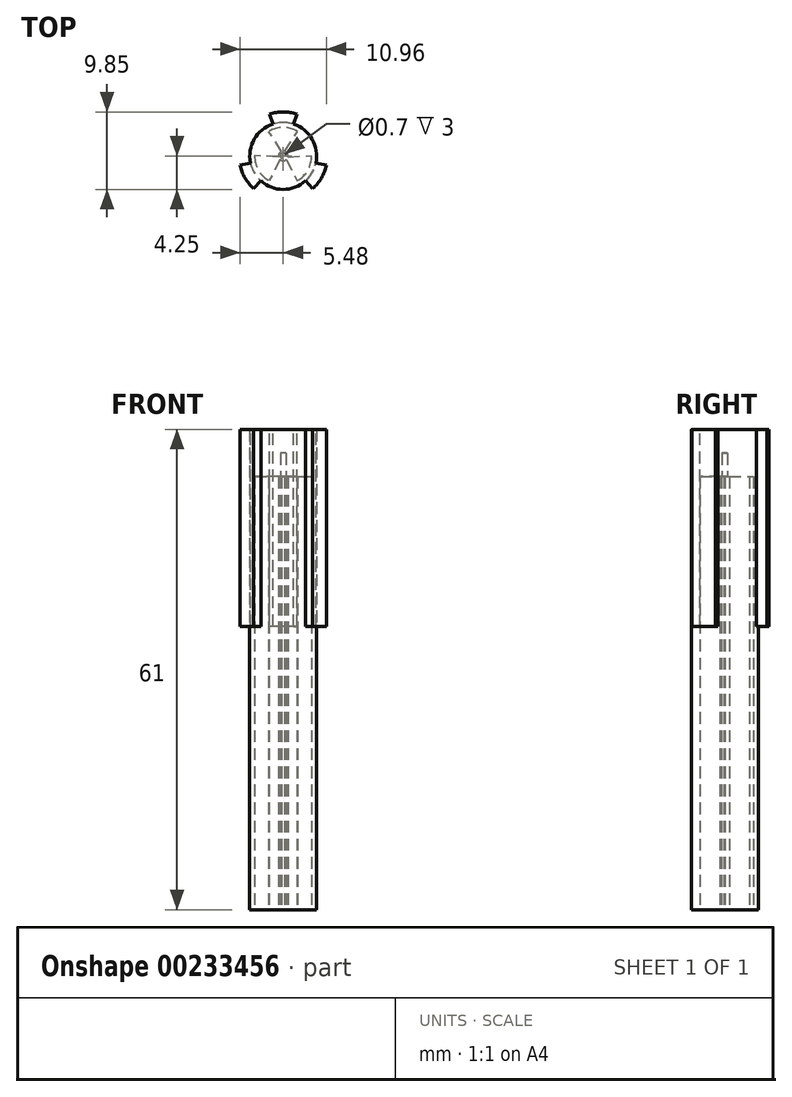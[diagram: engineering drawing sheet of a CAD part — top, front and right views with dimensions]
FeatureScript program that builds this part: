
annotation { "Feature Type Name" : "Feature", "Feature Type Description" : "" }
export const myFeature = defineFeature(function(context is Context, id is Id, definition is map)
    precondition{}
    {
        {
            var Q0;
            Q0=qCreatedBy(makeId("Top.planeOp"),FACE);
            var sketch = newSketch(context, id + "F0", { "sketchPlane" : qUnion([Q0])});
            skCircle(sketch, "E0", {"center": v(0, 0) * mm, "radius": 4.25 * mm});
            skArc(sketch, "E1", {"start": v(-0.4, -0.45) * mm, "mid": v(0, -0.6) * mm, "end": v(0.4, -0.45) * mm});
            skArc(sketch, "E2.trimOffspring", {"start": v(-0.19, 0.57) * mm, "mid": v(-0.52, 0.3) * mm, "end": v(-0.59, -0.12) * mm});
            skArc(sketch, "E3.trimOffspring", {"start": v(0.59, -0.12) * mm, "mid": v(0.52, 0.3) * mm, "end": v(0.19, 0.57) * mm});
            skArc(sketch, "E4.MirrorCS", {"start": v(-2.43, -2.7) * mm, "mid": v(-3.14, -1.81) * mm, "end": v(-3.55, -0.75) * mm});
            skLineSegment(sketch, "E5", {"start": v(0.4, -0.45) * mm, "end": v(1.78, -3.16) * mm});
            skLineSegment(sketch, "E6", {"start": v(0.59, -0.12) * mm, "end": v(3.62, 0.03) * mm});
            skLineSegment(sketch, "E7", {"start": v(0.19, 0.57) * mm, "end": v(1.84, 3.12) * mm});
            skLineSegment(sketch, "E8", {"start": v(-0.19, 0.57) * mm, "end": v(-1.84, 3.12) * mm});
            skLineSegment(sketch, "E9", {"start": v(-0.4, -0.45) * mm, "end": v(-1.78, -3.16) * mm});
            skLineSegment(sketch, "E10", {"start": v(-0.59, -0.12) * mm, "end": v(-3.62, 0.03) * mm});
            skArc(sketch, "E11", {"start": v(-3.62, 0.03) * mm, "mid": v(-3.6, -0.36) * mm, "end": v(-3.55, -0.75) * mm});
            skArc(sketch, "E12.trimOffspring", {"start": v(1.84, 3.12) * mm, "mid": v(0, 3.63) * mm, "end": v(-1.84, 3.12) * mm});
            skArc(sketch, "E13.trimOffspring", {"start": v(1.78, -3.16) * mm, "mid": v(3.14, -1.81) * mm, "end": v(3.62, 0.03) * mm});
            skPoint(sketch, "E14.end.orphan", {"position": v(3.55, -0.75) * mm});
            skPoint(sketch, "E14.start.orphan", {"position": v(2.43, -2.7) * mm});
            skArc(sketch, "E15.trimOffspring", {"start": v(-2.43, -2.7) * mm, "mid": v(-2.12, -2.94) * mm, "end": v(-1.78, -3.16) * mm});
            skSolve(sketch);
        }
        {
            var Q0;
            Q0 = qSketchRegion(id + "F0", true);
            extrude(context, id + "F1", {"entities" : qUnion([Q0]), "depth" : 55 * mm});
        }
        {
            var Q0;
            Q0=makeQuery(id+"F1.opExtrude","CAP_FACE",FACE,{"disambiguationData":[OSD([sQuery(id+"F0.wireOp",EDGE,"E0"),sQuery(id+"F0.wireOp",EDGE,"bDtTCxhL-HAn6-Tkzp-LlJu-NtYPpuUeie6u"),sQuery(id+"F0.wireOp",EDGE,"E1"),sQuery(id+"F0.wireOp",EDGE,"2EoDlAes-k3S6-9WM5-8KOT-6vRomLxSvBzK"),sQuery(id+"F0.wireOp",EDGE,"xVl7osAG-hVd3-mWhd-zs7N-79Gaa7jPuX8W"),sQuery(id+"F0.wireOp",EDGE,"tdh0X3bb-NIDe-KMIK-G8Cx-QX4AEOi9mbY9"),sQuery(id+"F0.wireOp",EDGE,"rWo34r8g-bj47-CR8p-qHGY-Ylw7Xh1i3jGK"),sQuery(id+"F0.wireOp",EDGE,"xJ7zvWuU-zeq0-NwZV-fpEs-XIAvMqc0LNuU"),sQuery(id+"F0.wireOp",EDGE,"a79hbzHv-ir01-oHMg-DY57-BzKwM4AU1gtr"),sQuery(id+"F0.wireOp",EDGE,"E2.trimOffspring"),sQuery(id+"F0.wireOp",EDGE,"6f2db6d1-0504-4149-804e-73a9b4ce37ea.trimOffspring"),sQuery(id+"F0.wireOp",EDGE,"bbb0789a-8a89-49f8-b75b-79ea315248d9.trimOffspring"),sQuery(id+"F0.wireOp",EDGE,"E3.trimOffspring")])],"isStart":false});
            var sketch = newSketch(context, id + "F2", { "sketchPlane" : qUnion([Q0])});
            skCircle(sketch, "E16", {"center": v(0, 0) * mm, "radius": 4.25 * mm});
            skCircle(sketch, "E17", {"center": v(0, 0) * mm, "radius": 0.35 * mm});
            skSolve(sketch);
        }
        {
            var Q0;
            Q0 = qSketchRegion(id + "F2", true);
            extrude(context, id + "F3", {"entities" : qUnion([Q0]), "operationType" : NewBodyOperationType.ADD, "depth" : 3 * mm});
        }
        {
            var Q0;
            Q0=makeQuery(id+"F3.opExtrude","CAP_FACE",FACE,{"disambiguationData":[OSD([sQuery(id+"F2.wireOp",EDGE,"E16"),sQuery(id+"F2.wireOp",EDGE,"E17")])],"isStart":false});
            var sketch = newSketch(context, id + "F4", { "sketchPlane" : qUnion([Q0])});
            skCircle(sketch, "E18", {"center": v(0, 0) * mm, "radius": 4.25 * mm});
            skSolve(sketch);
        }
        {
            var Q0;
            Q0 = qSketchRegion(id + "F4", true);
            extrude(context, id + "F5", {"entities" : qUnion([Q0]), "operationType" : NewBodyOperationType.ADD, "depth" : 3 * mm});
        }
        {
            var Q0;
            Q0=makeQuery(id+"F5.opExtrude","CAP_FACE",FACE,{"disambiguationData":[OSD([sQuery(id+"F4.wireOp",EDGE,"E18")])],"isStart":false});
            var sketch = newSketch(context, id + "F6", { "sketchPlane" : qUnion([Q0])});
            skArc(sketch, "E19", {"start": v(-4.16, -0.88) * mm, "mid": v(-3.68, -2.12) * mm, "end": v(-2.84, -3.16) * mm});
            skArc(sketch, "E20", {"start": v(-5.48, -1.16) * mm, "mid": v(-4.85, -2.8) * mm, "end": v(-3.75, -4.16) * mm});
            skLineSegment(sketch, "E21", {"start": v(1.31, 4.04) * mm, "end": v(1.73, 5.32) * mm});
            skLineSegment(sketch, "E22", {"start": v(-1.31, 4.04) * mm, "end": v(-1.73, 5.32) * mm});
            skLineSegment(sketch, "E23", {"start": v(2.84, -3.16) * mm, "end": v(3.75, -4.16) * mm});
            skLineSegment(sketch, "E24", {"start": v(4.16, -0.88) * mm, "end": v(5.48, -1.16) * mm});
            skLineSegment(sketch, "E25", {"start": v(-2.84, -3.16) * mm, "end": v(-3.75, -4.16) * mm});
            skLineSegment(sketch, "E26", {"start": v(-4.16, -0.88) * mm, "end": v(-5.48, -1.16) * mm});
            skArc(sketch, "E27.trimOffspring", {"start": v(1.73, 5.32) * mm, "mid": v(0, 5.6) * mm, "end": v(-1.73, 5.32) * mm});
            skArc(sketch, "E28.trimOffspring", {"start": v(3.75, -4.16) * mm, "mid": v(4.85, -2.8) * mm, "end": v(5.48, -1.16) * mm});
            skArc(sketch, "E29.trimOffspring", {"start": v(2.84, -3.16) * mm, "mid": v(3.68, -2.12) * mm, "end": v(4.16, -0.88) * mm});
            skArc(sketch, "E30.trimOffspring", {"start": v(1.31, 4.04) * mm, "mid": v(0, 4.25) * mm, "end": v(-1.31, 4.04) * mm});
            skSolve(sketch);
        }
        {
            var Q0;
            Q0 = qSketchRegion(id + "F6", true);
            extrude(context, id + "F7", {"entities" : qUnion([Q0]), "operationType" : NewBodyOperationType.ADD, "oppositeDirection" : true, "depth" : 25 * mm});
        }
    });
